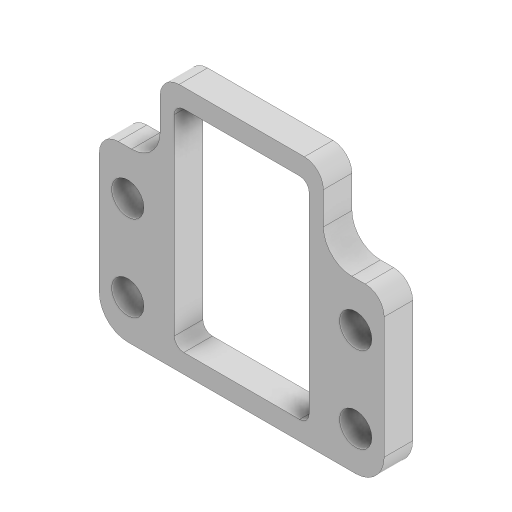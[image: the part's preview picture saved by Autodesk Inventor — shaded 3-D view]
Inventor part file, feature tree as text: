
AUTODESK INVENTOR PART (.ipt)
format: ipt  version: 2023 (Build 270158000, 158)  size: 167,936 bytes
history: native  units: mm
features: extrude x1, sketch x1
ambient origin geometry x8: Origin, YZ Plane, XZ Plane, XY Plane, X Axis, Y Axis, Z Axis, Center Point
bodies: Solid1 (feature_tree)
feature tree (2):
  extrude  "Extrusion1"  Depth=22.2mm
  sketch  "Sketch1"  dims[d0=14.2mm d1=22.2mm d2=1.0mm d3=7.1mm d4=11.1mm d5=3.4mm d6=20.0mm d8=9.0mm d9=20.0mm d11=24.0mm d14=0.0mm d15=12.0mm d16=3.0mm d17=3.0mm d18=2.0mm d19=2.0mm d20=3.0mm d21=3.0mm d22=0.0mm d23=1.5mm d24=3.0mm d25=3.0mm d26=2.0mm]
